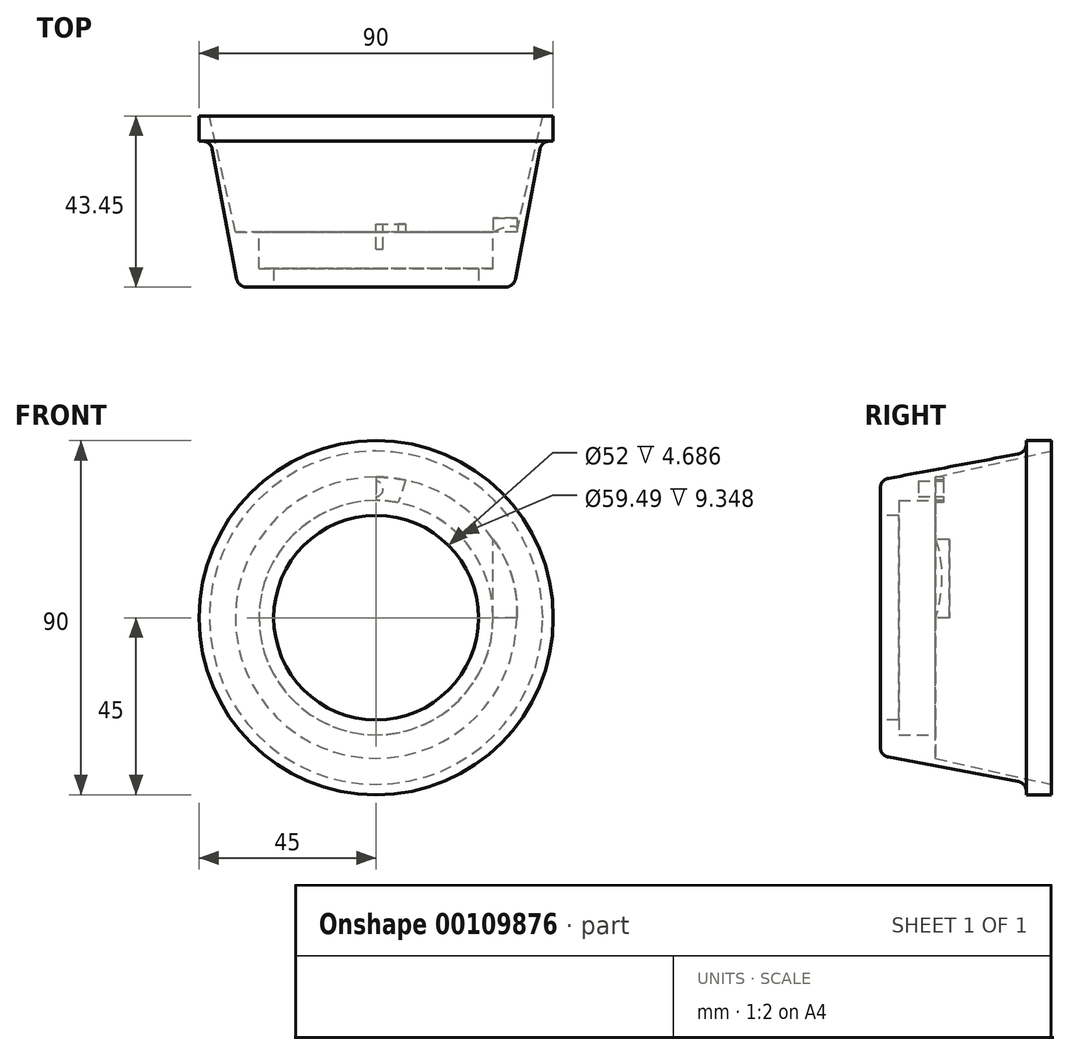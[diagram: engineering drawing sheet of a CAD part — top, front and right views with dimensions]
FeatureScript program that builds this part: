
annotation { "Feature Type Name" : "Feature", "Feature Type Description" : "" }
export const myFeature = defineFeature(function(context is Context, id is Id, definition is map)
    precondition{}
    {
        {
            var Q0;
            Q0=qCreatedBy(makeId("Front.planeOp"),FACE);
            var sketch = newSketch(context, id + "F0", { "sketchPlane" : qUnion([Q0])});
            skCircle(sketch, "E0", {"center": v(0, 0) * mm, "radius": 45 * mm});
            skSolve(sketch);
        }
        {
            var Q0;
            Q0=makeQuery(id+"F0.imprint","IMPRINT",FACE,{"disambiguationData":[TD([[makeQuery(id+"F0.imprint","IMPRINT",EDGE,{"derivedFrom":sQuery(id+"F0.wireOp",EDGE,"E0")}),1.0]])]});
            extrude(context, id + "F1", {"entities" : qUnion([Q0]), "depth" : 6.35 * mm});
        }
        {
            var Q0;
            Q0=qCreatedBy(makeId("Top.planeOp"),FACE);
            var sketch = newSketch(context, id + "F2", { "sketchPlane" : qUnion([Q0])});
            skLineSegment(sketch, "E1", {"start": v(0, -6.28) * mm, "end": v(0, -43.45) * mm});
            skLineSegment(sketch, "E2", {"start": v(0, -43.45) * mm, "end": v(-35, -43.45) * mm});
            skLineSegment(sketch, "E3", {"start": v(-35, -43.45) * mm, "end": v(-42, -6.32) * mm});
            skLineSegment(sketch, "E4", {"start": v(-42, -6.32) * mm, "end": v(0, -6.28) * mm});
            skLineSegment(sketch, "E5", {"start": v(0, -59.11) * mm, "end": v(0, 76.9) * mm, "construction": true});
            skSolve(sketch);
        }
        {
            var Q0;
            Q0 = qSketchRegion(id + "F2", true);
            var Q1;
            Q1=sQuery(id+"F2.wireOp",EDGE,"E5");
            revolve(context, id + "F3", {"operationType" : NewBodyOperationType.ADD, "entities" : qUnion([Q0]), "axis" : qUnion([Q1]), "revolveType" : RevolveType.FULL});
        }
        {
            var Q0;
            Q0=makeQuery(id+"F3.opRevolve","SWEPT_FACE",FACE,{"disambiguationData":[OSD([sQuery(id+"F2.wireOp",EDGE,"E2")])]});
            var sketch = newSketch(context, id + "F4", { "sketchPlane" : qUnion([Q0])});
            skCircle(sketch, "E6", {"center": v(0, 0) * mm, "radius": 26 * mm});
            skSolve(sketch);
        }
        {
            var Q0;
            Q0 = qSketchRegion(id + "F4", true);
            extrude(context, id + "F5", {"entities" : qUnion([Q0]), "operationType" : NewBodyOperationType.REMOVE, "oppositeDirection" : true, "depth" : 101.6 * mm});
        }
        {
            var Q0;
            Q0=makeQuery(id+"F3.boolean.opBoolean","INTERSECT",EDGE,{"derivedFrom":[makeQuery(id+"F1.opExtrude","CAP_FACE",FACE,{"disambiguationData":[OSD([sQuery(id+"F0.wireOp",EDGE,"E0")])],"isStart":false}),makeQuery(id+"F3.opRevolve","SWEPT_FACE",FACE,{"disambiguationData":[OSD([sQuery(id+"F2.wireOp",EDGE,"E3")])]})]});
            var Q1;
            Q1=makeQuery(id+"F3.opRevolve","SWEPT_EDGE",EDGE,{"disambiguationData":[OSD([sQuery(id+"F2.wireOp",EDGE,"E2"),sQuery(id+"F2.wireOp",EDGE,"E3")])]});
            fillet(context, id + "F6", {"entities" : qUnion([Q0, Q1]), "radius" : 2.54 * mm, "tangentPropagation" : true, "allowEdgeOverflow" : false});
        }
        {
            var Q0;
            Q0=qCreatedBy(makeId("Top.planeOp"),FACE);
            var sketch = newSketch(context, id + "F7", { "sketchPlane" : qUnion([Q0])});
            skLineSegment(sketch, "E7", {"start": v(-42.34, 0) * mm, "end": v(-35.74, -29.42) * mm});
            skLineSegment(sketch, "E8", {"start": v(-35.74, -29.42) * mm, "end": v(-29.75, -29.42) * mm});
            skLineSegment(sketch, "E9", {"start": v(-29.75, -29.42) * mm, "end": v(-29.75, -38.77) * mm});
            skLineSegment(sketch, "E10", {"start": v(-29.75, -38.77) * mm, "end": v(-24.75, -38.77) * mm});
            skLineSegment(sketch, "E11", {"start": v(-24.75, -38.77) * mm, "end": v(-24.75, -49.4) * mm});
            skLineSegment(sketch, "E12", {"start": v(-24.75, -49.4) * mm, "end": v(-15.76, -49.4) * mm});
            skLineSegment(sketch, "E13", {"start": v(-15.76, -49.4) * mm, "end": v(-15.76, -25.88) * mm});
            skLineSegment(sketch, "E14", {"start": v(-15.76, -25.88) * mm, "end": v(-26.2, 0) * mm});
            skLineSegment(sketch, "E15", {"start": v(0, -69.67) * mm, "end": v(0, 45.54) * mm, "construction": true});
            skLineSegment(sketch, "E16", {"start": v(-42.34, 0) * mm, "end": v(-42.34, 5.17) * mm});
            skLineSegment(sketch, "E17", {"start": v(-42.34, 5.17) * mm, "end": v(-26.1, 2.01) * mm});
            skLineSegment(sketch, "E18", {"start": v(-26.1, 2.01) * mm, "end": v(-26.2, 0) * mm});
            skSolve(sketch);
        }
        {
            var Q0;
            Q0 = qSketchRegion(id + "F7", true);
            var Q1;
            Q1=sQuery(id+"F7.wireOp",EDGE,"E15");
            revolve(context, id + "F8", {"operationType" : NewBodyOperationType.REMOVE, "entities" : qUnion([Q0]), "axis" : qUnion([Q1]), "revolveType" : RevolveType.FULL, "oppositeDirection" : true});
        }
        {
            var Q0;
            Q0=makeQuery(id+"F8.boolean.opBoolean","COPY",FACE,{"derivedFrom":makeQuery(id+"F8.opRevolve","SWEPT_FACE",FACE,{"disambiguationData":[OSD([sQuery(id+"F7.wireOp",EDGE,"E8")])]})});
            var sketch = newSketch(context, id + "F9", { "sketchPlane" : qUnion([Q0])});
            skLineSegment(sketch, "E19", {"start": v(-35.74, 0) * mm, "end": v(-29.75, 0) * mm});
            skLineSegment(sketch, "E20", {"start": v(-29.75, 0) * mm, "end": v(-29.75, 19.82) * mm});
            skArc(sketch, "E21", {"start": v(-29.75, 19.82) * mm, "mid": v(-34.54, 10.45) * mm, "end": v(-35.74, 0) * mm});
            skSolve(sketch);
        }
        {
            var Q0;
            Q0 = qSketchRegion(id + "F9", true);
            extrude(context, id + "F10", {"entities" : qUnion([Q0]), "operationType" : NewBodyOperationType.ADD, "depth" : 3.5 * mm});
        }
        {
            var Q0;
            Q0=qCreatedBy(makeId("Front.planeOp"),FACE);
            var sketch = newSketch(context, id + "F11", { "sketchPlane" : qUnion([Q0])});
            skCircle(sketch, "E22", {"center": v(0, 0) * mm, "radius": 28.6 * mm});
            skSolve(sketch);
        }
        {
            var Q0;
            Q0 = qSketchRegion(id + "F11", true);
            extrude(context, id + "F12", {"entities" : qUnion([Q0]), "operationType" : NewBodyOperationType.REMOVE, "depth" : 5.08 * mm});
        }
        {
            var Q0;
            Q0=makeQuery(id+"F8.boolean.opBoolean","COPY",FACE,{"derivedFrom":makeQuery(id+"F8.opRevolve","SWEPT_FACE",FACE,{"disambiguationData":[OSD([sQuery(id+"F7.wireOp",EDGE,"E8")])]})});
            var sketch = newSketch(context, id + "F13", { "sketchPlane" : qUnion([Q0])});
            skLineSegment(sketch, "E23", {"start": v(0, 35.74) * mm, "end": v(0, 29.75) * mm});
            skLineSegment(sketch, "E24", {"start": v(-7.5, 34.95) * mm, "end": v(-5.6, 29.22) * mm});
            skArc(sketch, "E25", {"start": v(0, 35.74) * mm, "mid": v(-3.78, 35.54) * mm, "end": v(-7.5, 34.95) * mm});
            skArc(sketch, "E26", {"start": v(0, 29.75) * mm, "mid": v(-2.8, 29.6) * mm, "end": v(-5.6, 29.22) * mm});
            skSolve(sketch);
        }
        {
            var Q0;
            Q0 = qSketchRegion(id + "F13", true);
            extrude(context, id + "F14", {"entities" : qUnion([Q0]), "operationType" : NewBodyOperationType.ADD, "depth" : 2 * mm});
        }
        {
            var Q0;
            Q0=makeQuery(id+"F14.opExtrude","CAP_FACE",FACE,{"disambiguationData":[OSD([sQuery(id+"F13.wireOp",EDGE,"E23"),sQuery(id+"F13.wireOp",EDGE,"E24"),sQuery(id+"F13.wireOp",EDGE,"E25"),sQuery(id+"F13.wireOp",EDGE,"E26")])],"isStart":false});
            var sketch = newSketch(context, id + "F15", { "sketchPlane" : qUnion([Q0])});
            skLineSegment(sketch, "E27", {"start": v(0, 35.74) * mm, "end": v(0, 34.74) * mm});
            skLineSegment(sketch, "E28", {"start": v(0, 29.75) * mm, "end": v(0, 30.75) * mm});
            skArc(sketch, "E29", {"start": v(0, 34.74) * mm, "mid": v(-1.8, 32.74) * mm, "end": v(0, 30.75) * mm});
            skLineSegment(sketch, "E30", {"start": v(0, 34.74) * mm, "end": v(0, 30.75) * mm});
            skSolve(sketch);
        }
        {
            var Q0;
            Q0 = qSketchRegion(id + "F15", true);
            extrude(context, id + "F16", {"entities" : qUnion([Q0]), "operationType" : NewBodyOperationType.REMOVE, "oppositeDirection" : true, "depth" : 6.35 * mm});
        }
    });
